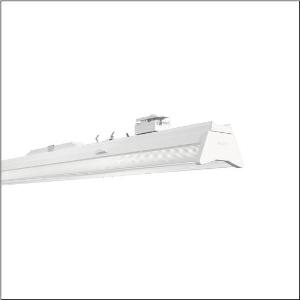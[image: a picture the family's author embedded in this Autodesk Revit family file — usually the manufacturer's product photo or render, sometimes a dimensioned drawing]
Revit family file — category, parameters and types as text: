
# Revit family: licross_r__21_performance_mo_52td16cn46xg_4d89
name_source: partatom
category: Lighting Fixtures
units: mm (PartAtom-declared; Revit-internal decimal feet)

## family parameters
Cut with Voids When Loaded = No
Host = Face
Light Source = No
Part Type = Normal
Room Calculation Point = No
Round Connector Dimension = Use Diameter
Shared = No

## types (1)
- --- (1 x LED, 6000 lm, 32 W, 4000K)
    Apparent Load = 32 VA
    CIE Flux Codes = 66 88 96 79 100
    Color Rendering = 80
    Color Temperature = 4000K
    Default Elevation = 1800 mm
    Description = Licross® 21 Performance MO, luminaire insert, of sheet steel, galvanised, coil coated, white, length: 1.500mm, width: 120mm, height: 123mm, LED rated luminous flux: 6.000lm, light colour: 840, control gear: ON/OFF Multilumen, CLOi, control gear: ECG Multilumen, with plug, 3-pole, with phase selection, mains connection: 220..240V, AC, 50/60Hz, start of lifetime: 32W, end of service life: 38W, halogen-free wiring, primary light control with lens, of plastic, primary optical cover: cover, of PMMA, light emission: direct/indirect distribution, primary light characteristic: symmetric, protection rating (complete): IP54, insulation class (complete): insulation class I (protective earthing), certification: CE, ENEC, UKCA, protection symbol: D if used in an environment with non-conductive dust loads with corresponding accessories, impact resistance: IK06, permissible ambient temperature for indoor applications: -35..+55°C, corresponds to IFS (International Featured Standards) requirements for safety and quality in the food industry, reducing of maximum allowable ambient temperature of 5°C with ceiling mounting, LABS conformity tested according to VDMA 24364:2018-05, packaging unit: 1 piece
    Height = 114 mm
    Lamp = 1 x LED
    Lamp Light Flux = 6000 lm
    Lamp Power = 32 W
    Lamp count = 1
    Length = 1500 mm
    Luminous efficacy = 188 lm/W
    Manufacturer = Siteco
    ModVariant = No
    Model = 52TD16CN46XG
    Mounting Place = Ceiling
    Mounting Type = Pendant
    Number of Poles = 1
    OnlyDefault = Yes
    Power Factor = 1
    Product Name = Licross® 21 Performance MO
    Product group = luminaire insert
    ProductGroupID = 901
    Protection Class = Protection class I
    Protection Degree = IP 54
    RLX_Detail_Level = 1
    RLX_Emergency_Light_Flux = 0 lm
    RLX_Emergency_Type = 0
    RLX_Emergency_Type_DB = No
    RlxData = <blob elided: 31817 chars, md5=eb9e5b99>
    Socket = socket
    Standby Power = 0 W
    System Light Flux = 6000 lm
    System Power = 32 W
    Type Comments = factory setting: luminous flux: 100 % | (A | C | E) | 74 mA
    Type Image = l_1256138.jpg
    URL = http://relux.com
    VarID = @adj_041633
    Voltage = 0 V
    Weight = 0.00 kg
    Width = 120 mm

## geometry (parser evidence)
native form markers: Blend x4, Sweep x11
no freeform markers — native parametric forms only
